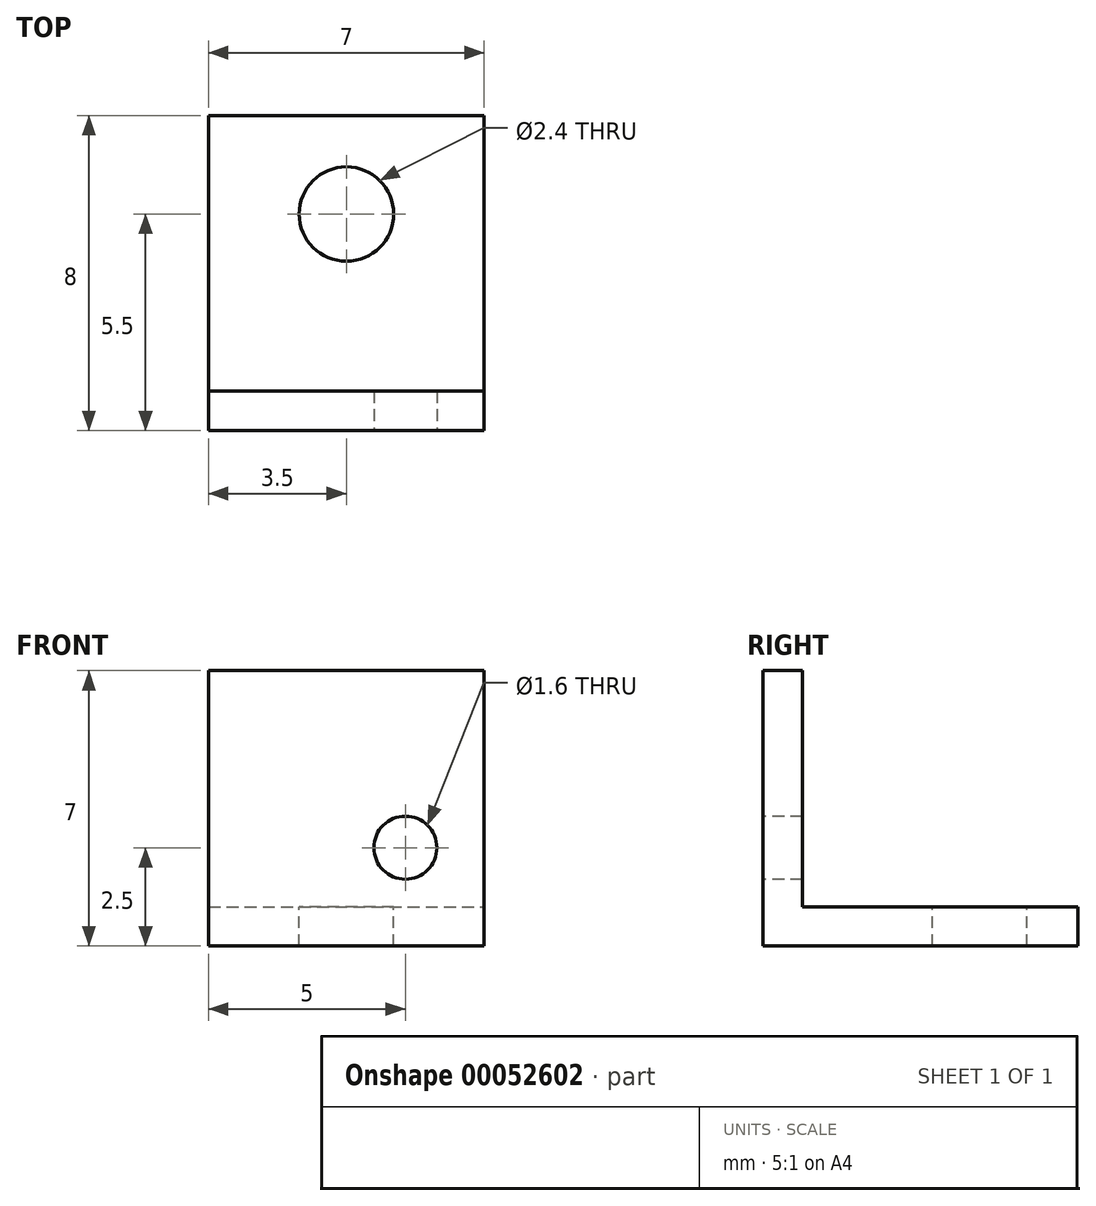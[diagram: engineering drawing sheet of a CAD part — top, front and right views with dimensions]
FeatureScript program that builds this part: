
annotation { "Feature Type Name" : "Feature", "Feature Type Description" : "" }
export const myFeature = defineFeature(function(context is Context, id is Id, definition is map)
    precondition{}
    {
        {
            var Q0;
            Q0=qCreatedBy(makeId("Top.planeOp"),FACE);
            var sketch = newSketch(context, id + "F0", { "sketchPlane" : qUnion([Q0])});
            skLineSegment(sketch, "E0.bottom", {"start": v(0, 0) * mm, "end": v(7, 0) * mm});
            skLineSegment(sketch, "E0.top", {"start": v(0, 8) * mm, "end": v(7, 8) * mm});
            skLineSegment(sketch, "E0.left", {"start": v(0, 0) * mm, "end": v(0, 8) * mm});
            skLineSegment(sketch, "E0.right", {"start": v(7, 0) * mm, "end": v(7, 8) * mm});
            skSolve(sketch);
        }
        {
            var Q0;
            Q0 = qSketchRegion(id + "F0", true);
            extrude(context, id + "F1", {"entities" : qUnion([Q0]), "depth" : 1 * mm});
        }
        {
            var Q0;
            Q0=makeQuery(id+"F1.opExtrude","CAP_FACE",FACE,{"disambiguationData":[OSD([sQuery(id+"F0.wireOp",EDGE,"E0.bottom"),sQuery(id+"F0.wireOp",EDGE,"E0.top"),sQuery(id+"F0.wireOp",EDGE,"E0.left"),sQuery(id+"F0.wireOp",EDGE,"E0.right")])],"isStart":false});
            var sketch = newSketch(context, id + "F2", { "sketchPlane" : qUnion([Q0])});
            skLineSegment(sketch, "E1.bottom", {"start": v(0, 0) * mm, "end": v(7, 0) * mm});
            skLineSegment(sketch, "E1.top", {"start": v(0, 1) * mm, "end": v(7, 1) * mm});
            skLineSegment(sketch, "E1.left", {"start": v(0, 0) * mm, "end": v(0, 1) * mm});
            skLineSegment(sketch, "E1.right", {"start": v(7, 0) * mm, "end": v(7, 1) * mm});
            skSolve(sketch);
        }
        {
            var Q0;
            Q0 = qSketchRegion(id + "F2", true);
            extrude(context, id + "F3", {"entities" : qUnion([Q0]), "operationType" : NewBodyOperationType.ADD, "depth" : 6 * mm});
        }
        {
            var Q0;
            Q0=makeQuery(id+"F1.opExtrude","CAP_FACE",FACE,{"disambiguationData":[OSD([sQuery(id+"F0.wireOp",EDGE,"E0.bottom"),sQuery(id+"F0.wireOp",EDGE,"E0.top"),sQuery(id+"F0.wireOp",EDGE,"E0.left"),sQuery(id+"F0.wireOp",EDGE,"E0.right")])],"isStart":false});
            var sketch = newSketch(context, id + "F4", { "sketchPlane" : qUnion([Q0])});
            skPoint(sketch, "E2", {"position": v(3.5, 5.5) * mm});
            skLineSegment(sketch, "E3", {"start": v(3.5, 5.5) * mm, "end": v(7, 5.5) * mm});
            skLineSegment(sketch, "E4", {"start": v(3.5, 5.5) * mm, "end": v(0, 5.5) * mm});
            skSolve(sketch);
        }
        {
            var Q0;
            Q0=sQuery(id+"F4.wireOp",VERTEX,"E2");
            var Q1;
            Q1=makeQuery(id+"F1.opExtrude","SWEPT_BODY",BODY,{"disambiguationData":[OSD([sQuery(id+"F0.wireOp",EDGE,"E0.bottom"),sQuery(id+"F0.wireOp",EDGE,"E0.top"),sQuery(id+"F0.wireOp",EDGE,"E0.left"),sQuery(id+"F0.wireOp",EDGE,"E0.right")])]});
            hole(context, id + "F5", {"style" : HoleStyle.SIMPLE, "holeDiameter" : 2.4 * mm, "endStyle" : HoleEndStyle.THROUGH, "locations" : qUnion([Q0]), "scope" : qUnion([Q1])});
        }
        {
            var Q0;
            Q0=makeQuery(id+"F3.boolean.opBoolean","MERGE",FACE,{"derivedFrom":[makeQuery(id+"F1.opExtrude","SWEPT_FACE",FACE,{"disambiguationData":[OSD([sQuery(id+"F0.wireOp",EDGE,"E0.bottom")])]}),makeQuery(id+"F3.opExtrude","SWEPT_FACE",FACE,{"disambiguationData":[OSD([sQuery(id+"F2.wireOp",EDGE,"E1.bottom")])]})]});
            var sketch = newSketch(context, id + "F6", { "sketchPlane" : qUnion([Q0])});
            skPoint(sketch, "E5", {"position": v(5, 2.5) * mm});
            skSolve(sketch);
        }
        {
            var Q0;
            Q0=sQuery(id+"F6.wireOp",VERTEX,"E5");
            var Q1;
            Q1=makeQuery(id+"F1.opExtrude","SWEPT_BODY",BODY,{"disambiguationData":[OSD([sQuery(id+"F0.wireOp",EDGE,"E0.bottom"),sQuery(id+"F0.wireOp",EDGE,"E0.top"),sQuery(id+"F0.wireOp",EDGE,"E0.left"),sQuery(id+"F0.wireOp",EDGE,"E0.right")])]});
            hole(context, id + "F7", {"style" : HoleStyle.SIMPLE, "holeDiameter" : 1.6 * mm, "endStyle" : HoleEndStyle.THROUGH, "locations" : qUnion([Q0]), "scope" : qUnion([Q1])});
        }
    });
